# Revit family: Specialty_Equipment-Planter-Planters_Unlimited-Modern-Round-bk5
name_source: partatom
category: Specialty Equipment
units: mm (PartAtom-declared; Revit-internal decimal feet)

## family parameters
Always vertical = Yes
Cut with Voids When Loaded = No
OmniClass Number = 23.40.05.21.17
OmniClass Title = Planters
Part Type = Normal
Room Calculation Point = No
Round Connector Dimension = Use Diameter
Shared = No
Work Plane-Based = No

## types (1)
- default load type catalog
    Assembly Code = G2050600
    CD_Caster Set = Yes
    CD_Diameter = 2' - 0"
    CD_Diameter Max = 6' - 0"
    CD_Diameter Min = 1' - 6"
    CD_Finish = Plastic-Fiberglass-Carlsbad-Semi_Gloss-Charcoal
    CD_Height = 2' - 0"
    CD_Height Max = 4' - 0"
    CD_Height Min = 1' - 6"
    CD_Microsite = https://www.caddetails.com
    CD_Offset = 0' - 0"
    CD_Product Page URL = https://www.plantersunlimited.com
    CD_Requested Diameter = 2' - 0"
    CD_Requested Height = 2' - 0"
    CD_Specification = https://www.plantersunlimited.com
    Default Elevation = 0' - 0"
    Description = Modular Planting Bed
    Manufacturer = Planters Unlimited
    Model = Modern Series Planters
    Type Comments = Round Planter
    URL = https://www.plantersunlimited.com

## geometry (parser evidence)
native form markers: Sweep x5
no freeform markers — native parametric forms only
